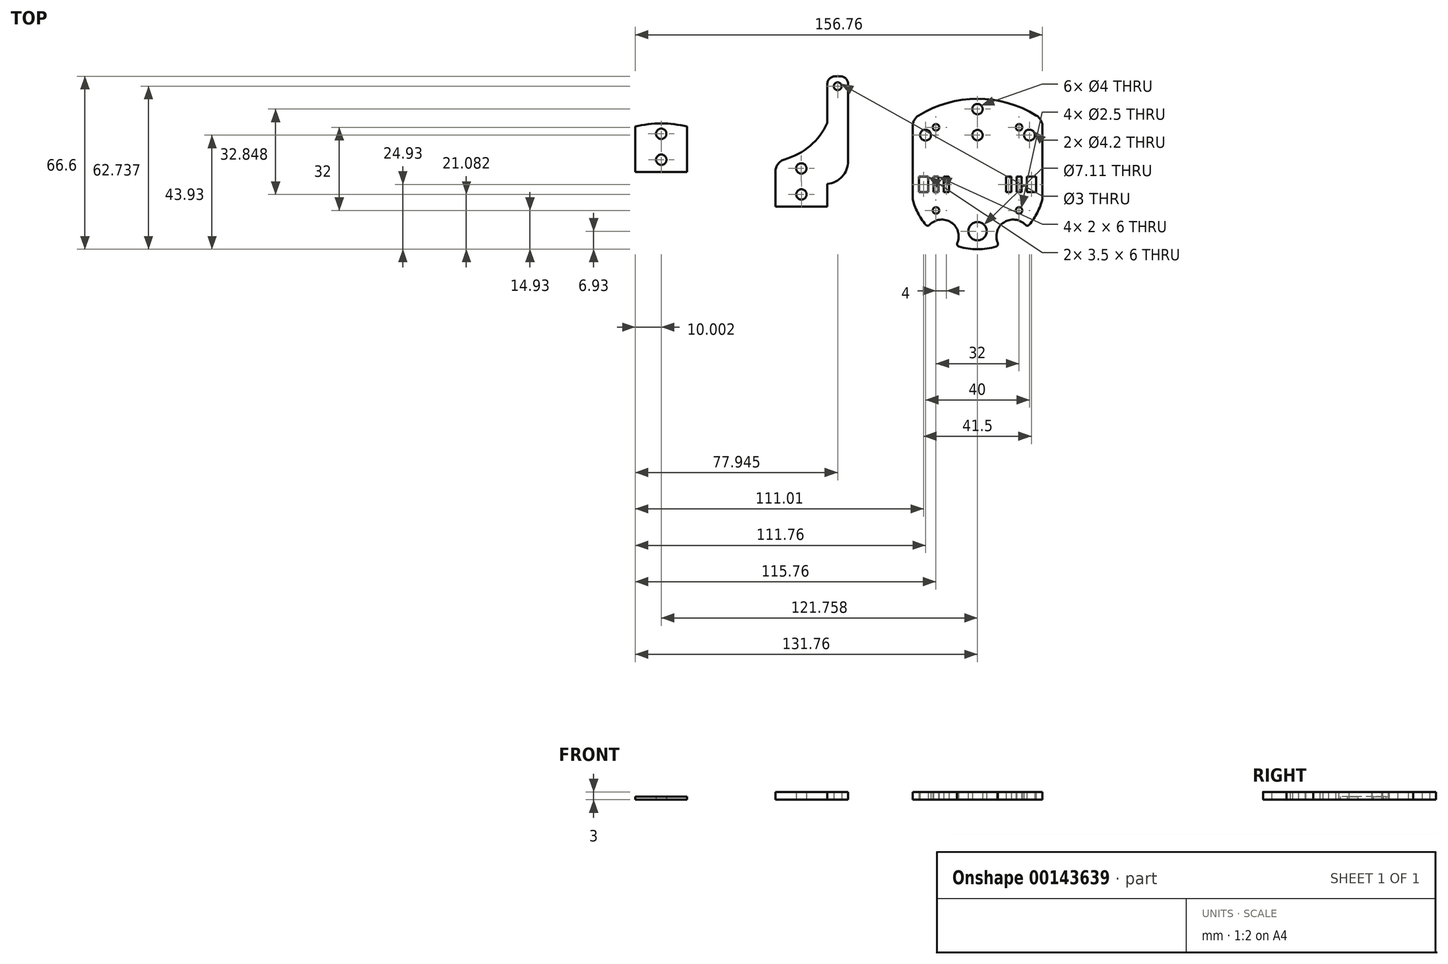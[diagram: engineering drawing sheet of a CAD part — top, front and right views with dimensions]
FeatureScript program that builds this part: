
annotation { "Feature Type Name" : "Feature", "Feature Type Description" : "" }
export const myFeature = defineFeature(function(context is Context, id is Id, definition is map)
    precondition{}
    {
        {
            var Q0;
            Q0=qCreatedBy(makeId("Top.planeOp"),FACE);
            var sketch = newSketch(context, id + "F0", { "sketchPlane" : qUnion([Q0])});
            skPoint(sketch, "E0.middle", {"position": v(0, 0) * mm});
            skLineSegment(sketch, "E1.top", {"start": v(-25, -10.03) * mm, "end": v(22.32, -10.03) * mm, "construction": true});
            skLineSegment(sketch, "E2.bottom", {"start": v(-20, 19) * mm, "end": v(20, 19) * mm, "construction": true});
            skCircle(sketch, "E3", {"center": v(-20, 19) * mm, "radius": 10 * mm, "construction": true});
            skCircle(sketch, "E4", {"center": v(0, -18) * mm, "radius": 10 * mm, "construction": true});
            skLineSegment(sketch, "E5.left", {"start": v(-25, 22.31) * mm, "end": v(-25, -5.6) * mm});
            skLineSegment(sketch, "E5.right", {"start": v(25, 22.31) * mm, "end": v(25, -5.6) * mm});
            skCircle(sketch, "E6", {"center": v(0, -18) * mm, "radius": 3.56 * mm});
            skCircle(sketch, "E7", {"center": v(-20, 19) * mm, "radius": 2.1 * mm});
            skCircle(sketch, "E8", {"center": v(20, 19) * mm, "radius": 2.1 * mm});
            skLineSegment(sketch, "E9", {"start": v(0, 0) * mm, "end": v(-25, 0) * mm, "construction": true});
            skLineSegment(sketch, "E10", {"start": v(0, 0) * mm, "end": v(0, 25) * mm, "construction": true});
            skLineSegment(sketch, "E11.bottom", {"start": v(-19, 3) * mm, "end": v(-22.5, 3) * mm});
            skLineSegment(sketch, "E11.top", {"start": v(-19, -3) * mm, "end": v(-22.5, -3) * mm});
            skLineSegment(sketch, "E11.left", {"start": v(-19, 3) * mm, "end": v(-19, -3) * mm});
            skLineSegment(sketch, "E11.right", {"start": v(-22.5, 3) * mm, "end": v(-22.5, -3) * mm});
            skPoint(sketch, "E11.middle", {"position": v(-20.75, 0) * mm});
            skLineSegment(sketch, "E12.bottom", {"start": v(-15, 3) * mm, "end": v(-17, 3) * mm});
            skLineSegment(sketch, "E12.top", {"start": v(-15, -3) * mm, "end": v(-17, -3) * mm});
            skLineSegment(sketch, "E12.left", {"start": v(-15, 3) * mm, "end": v(-15, -3) * mm});
            skLineSegment(sketch, "E12.right", {"start": v(-17, 3) * mm, "end": v(-17, -3) * mm});
            skPoint(sketch, "E12.middle", {"position": v(-16, 0) * mm});
            skLineSegment(sketch, "E13.bottom", {"start": v(-13, 3) * mm, "end": v(-11, 3) * mm});
            skLineSegment(sketch, "E13.top", {"start": v(-13, -3) * mm, "end": v(-11, -3) * mm});
            skLineSegment(sketch, "E13.left", {"start": v(-13, 3) * mm, "end": v(-13, -3) * mm});
            skLineSegment(sketch, "E13.right", {"start": v(-11, 3) * mm, "end": v(-11, -3) * mm});
            skPoint(sketch, "E13.middle", {"position": v(-12, 0) * mm});
            skLineSegment(sketch, "E14.MirrorCS", {"start": v(15, 3) * mm, "end": v(17, 3) * mm});
            skLineSegment(sketch, "E15.MirrorCS", {"start": v(13, -3) * mm, "end": v(11, -3) * mm});
            skLineSegment(sketch, "E16.MirrorCS", {"start": v(11, 3) * mm, "end": v(11, -3) * mm});
            skLineSegment(sketch, "E17.MirrorCS", {"start": v(13, 3) * mm, "end": v(11, 3) * mm});
            skPoint(sketch, "E18.MirrorP", {"position": v(16, 0) * mm});
            skLineSegment(sketch, "E19.MirrorCS", {"start": v(0, 0) * mm, "end": v(25, 0) * mm, "construction": true});
            skLineSegment(sketch, "E20.MirrorCS", {"start": v(22.5, 3) * mm, "end": v(22.5, -3) * mm});
            skLineSegment(sketch, "E21.MirrorCS", {"start": v(13, 3) * mm, "end": v(13, -3) * mm});
            skLineSegment(sketch, "E22.MirrorCS", {"start": v(15, 3) * mm, "end": v(15, -3) * mm});
            skLineSegment(sketch, "E23.MirrorCS", {"start": v(19, 3) * mm, "end": v(22.5, 3) * mm});
            skPoint(sketch, "E24.MirrorP", {"position": v(12, 0) * mm});
            skLineSegment(sketch, "E25.MirrorCS", {"start": v(19, 3) * mm, "end": v(19, -3) * mm});
            skLineSegment(sketch, "E26.MirrorCS", {"start": v(17, 3) * mm, "end": v(17, -3) * mm});
            skPoint(sketch, "E27.MirrorP", {"position": v(20.75, 0) * mm});
            skLineSegment(sketch, "E28.MirrorCS", {"start": v(19, -3) * mm, "end": v(22.5, -3) * mm});
            skLineSegment(sketch, "E29", {"start": v(15, -3) * mm, "end": v(17, -3) * mm});
            skCircle(sketch, "E30", {"center": v(0, 19) * mm, "radius": 2 * mm});
            skCircle(sketch, "E31", {"center": v(0, 29) * mm, "radius": 2 * mm});
            skLineSegment(sketch, "E32", {"start": v(0, 25) * mm, "end": v(0, 29) * mm, "construction": true});
            skArc(sketch, "E33", {"start": v(22.62, 26.57) * mm, "mid": v(0, 32.96) * mm, "end": v(-22.62, 26.57) * mm});
            skPoint(sketch, "E34", {"position": v(-20, 9) * mm});
            skPoint(sketch, "E35", {"position": v(-20, 10) * mm});
            skPoint(sketch, "E36.visualSharp", {"position": v(-25, -10.03) * mm});
            skPoint(sketch, "E37.visualSharp", {"position": v(-8, -24) * mm});
            skPoint(sketch, "E38", {"position": v(0, -8) * mm});
            skPoint(sketch, "E39", {"position": v(0, -10) * mm});
            skPoint(sketch, "E40.visualSharp", {"position": v(-25, 25) * mm});
            skArc(sketch, "E40.filletArc", {"start": v(-22.62, 26.57) * mm, "mid": v(-24.36, 24.75) * mm, "end": v(-25, 22.31) * mm});
            skPoint(sketch, "E41.visualSharp", {"position": v(25, 25) * mm});
            skArc(sketch, "E41.filletArc", {"start": v(25, 22.31) * mm, "mid": v(24.36, 24.75) * mm, "end": v(22.62, 26.57) * mm});
            skLineSegment(sketch, "E42.bottom", {"start": v(16, 22) * mm, "end": v(-16, 22) * mm, "construction": true});
            skLineSegment(sketch, "E42.top", {"start": v(16, -10) * mm, "end": v(-16, -10) * mm, "construction": true});
            skLineSegment(sketch, "E42.left", {"start": v(16, 22) * mm, "end": v(16, -10) * mm, "construction": true});
            skLineSegment(sketch, "E42.right", {"start": v(-16, 22) * mm, "end": v(-16, -10) * mm, "construction": true});
            skPoint(sketch, "E42.middle", {"position": v(0, 6) * mm});
            skCircle(sketch, "E43", {"center": v(-16, -10) * mm, "radius": 1.25 * mm});
            skCircle(sketch, "E44", {"center": v(16, -10) * mm, "radius": 1.25 * mm});
            skCircle(sketch, "E45", {"center": v(16, 22) * mm, "radius": 1.25 * mm});
            skCircle(sketch, "E46", {"center": v(-16, 22) * mm, "radius": 1.25 * mm});
            skPoint(sketch, "E47.orphan", {"position": v(25, -10.03) * mm});
            skPoint(sketch, "E48.orphan", {"position": v(8, -24) * mm});
            skLineSegment(sketch, "E49", {"start": v(-25, 14.31) * mm, "end": v(25, 14.31) * mm});
            skPoint(sketch, "E50.visualSharp", {"position": v(-21.13, -10.47) * mm});
            skArc(sketch, "E51", {"start": v(-25, -5.6) * mm, "mid": v(-23.01, -10.83) * mm, "end": v(-19.94, -15.51) * mm});
            skLineSegment(sketch, "E52", {"start": v(0, -18) * mm, "end": v(0, -24.93) * mm, "construction": true});
            skArc(sketch, "E53", {"start": v(0, -24.93) * mm, "mid": v(3.6, -24.67) * mm, "end": v(7.14, -23.92) * mm});
            skArc(sketch, "E54", {"start": v(-7.79, -22.56) * mm, "mid": v(-10.18, -14.59) * mm, "end": v(-18.44, -15.56) * mm});
            skArc(sketch, "E55.MirrorCS", {"start": v(7.79, -22.56) * mm, "mid": v(10.18, -14.59) * mm, "end": v(18.44, -15.56) * mm});
            skArc(sketch, "E56.trimOffspring", {"start": v(-7.14, -23.92) * mm, "mid": v(-3.6, -24.67) * mm, "end": v(0, -24.93) * mm});
            skArc(sketch, "E57.trimOffspring", {"start": v(19.94, -15.51) * mm, "mid": v(23.01, -10.83) * mm, "end": v(25, -5.6) * mm});
            skPoint(sketch, "E58.visualSharp", {"position": v(-19.14, -16.44) * mm});
            skArc(sketch, "E58.filletArc", {"start": v(-19.94, -15.51) * mm, "mid": v(-19.2, -15.88) * mm, "end": v(-18.44, -15.56) * mm});
            skPoint(sketch, "E59.visualSharp", {"position": v(-8.32, -23.55) * mm});
            skArc(sketch, "E59.filletArc", {"start": v(-7.79, -22.56) * mm, "mid": v(-7.77, -23.38) * mm, "end": v(-7.14, -23.92) * mm});
            skPoint(sketch, "E60.visualSharp", {"position": v(8.32, -23.55) * mm});
            skArc(sketch, "E60.filletArc", {"start": v(7.14, -23.92) * mm, "mid": v(7.77, -23.38) * mm, "end": v(7.79, -22.56) * mm});
            skPoint(sketch, "E61.visualSharp", {"position": v(19.14, -16.44) * mm});
            skArc(sketch, "E61.filletArc", {"start": v(18.44, -15.56) * mm, "mid": v(19.2, -15.88) * mm, "end": v(19.94, -15.51) * mm});
            skCircle(sketch, "E62", {"center": v(-121.74, 9.5) * mm, "radius": 2 * mm});
            skCircle(sketch, "E63", {"center": v(-121.76, 19.5) * mm, "radius": 2 * mm});
            skLineSegment(sketch, "E64", {"start": v(-121.76, 15.5) * mm, "end": v(-121.76, 19.5) * mm, "construction": true});
            skArc(sketch, "E65", {"start": v(-111.76, 22.3) * mm, "mid": v(-121.76, 23.47) * mm, "end": v(-131.76, 22.3) * mm});
            skLineSegment(sketch, "E66", {"start": v(-131.76, 4.82) * mm, "end": v(-111.76, 4.82) * mm});
            skLineSegment(sketch, "E67.left", {"start": v(-111.76, 22.3) * mm, "end": v(-111.76, 4.82) * mm});
            skLineSegment(sketch, "E67.right", {"start": v(-131.76, 22.3) * mm, "end": v(-131.76, 4.82) * mm});
            skPoint(sketch, "E67.middle", {"position": v(-121.76, 15.5) * mm});
            skCircle(sketch, "E68", {"center": v(-67.8, -3.85) * mm, "radius": 2 * mm});
            skCircle(sketch, "E69", {"center": v(-67.81, 6.15) * mm, "radius": 2 * mm});
            skLineSegment(sketch, "E70", {"start": v(-67.81, 2.15) * mm, "end": v(-67.81, 6.15) * mm, "construction": true});
            skLineSegment(sketch, "E71", {"start": v(-77.81, -8.53) * mm, "end": v(-57.81, -8.53) * mm});
            skLineSegment(sketch, "E72.left", {"start": v(-57.81, 0.2) * mm, "end": v(-57.81, -8.53) * mm});
            skLineSegment(sketch, "E72.right", {"start": v(-77.81, 4.87) * mm, "end": v(-77.81, -8.53) * mm});
            skPoint(sketch, "E72.middle", {"position": v(-67.81, 2.15) * mm});
            skLineSegment(sketch, "E73.top", {"start": v(-54.81, 41.67) * mm, "end": v(-52.81, 41.67) * mm});
            skLineSegment(sketch, "E73.left", {"start": v(-57.81, 23.67) * mm, "end": v(-57.81, 38.67) * mm});
            skLineSegment(sketch, "E73.right", {"start": v(-49.81, 8.94) * mm, "end": v(-49.81, 38.67) * mm});
            skCircle(sketch, "E74", {"center": v(-53.81, 37.8) * mm, "radius": 1.5 * mm});
            skPoint(sketch, "E74.centerSnap0", {"position": v(-53.81, 41.67) * mm});
            skPoint(sketch, "E75.orphan", {"position": v(-57.81, 5.67) * mm});
            skArc(sketch, "E76", {"start": v(-74.16, 9.68) * mm, "mid": v(-64.45, 14.87) * mm, "end": v(-57.81, 23.67) * mm});
            skArc(sketch, "E77", {"start": v(-57.81, 0.2) * mm, "mid": v(-52.12, 3.02) * mm, "end": v(-49.81, 8.94) * mm});
            skPoint(sketch, "E78.visualSharp", {"position": v(-77.81, 8.94) * mm});
            skArc(sketch, "E78.filletArc", {"start": v(-74.16, 9.68) * mm, "mid": v(-76.8, 7.9) * mm, "end": v(-77.81, 4.87) * mm});
            skPoint(sketch, "E79.visualSharp", {"position": v(-57.81, 41.67) * mm});
            skArc(sketch, "E79.filletArc", {"start": v(-54.81, 41.67) * mm, "mid": v(-56.94, 40.79) * mm, "end": v(-57.81, 38.67) * mm});
            skPoint(sketch, "E80.visualSharp", {"position": v(-49.81, 41.67) * mm});
            skArc(sketch, "E80.filletArc", {"start": v(-49.81, 38.67) * mm, "mid": v(-50.7, 40.79) * mm, "end": v(-52.81, 41.67) * mm});
            skSolve(sketch);
        }
        {
            var Q0;
            Q0=makeQuery(id+"F0.imprint","IMPRINT",FACE,{"disambiguationData":[TD([[makeQuery(id+"F0.imprint","IMPRINT",EDGE,{"derivedFrom":sQuery(id+"F0.wireOp",EDGE,"E6")}),-1.0]])]});
            var Q1;
            Q1=makeQuery(id+"F0.imprint","IMPRINT",FACE,{"disambiguationData":[TD([[makeQuery(id+"F0.imprint","IMPRINT",EDGE,{"derivedFrom":sQuery(id+"F0.wireOp",EDGE,"E7")}),-1.0]])]});
            var Q2;
            Q2=makeQuery(id+"F0.imprint","IMPRINT",FACE,{"disambiguationData":[TD([[makeQuery(id+"F0.imprint","IMPRINT",EDGE,{"derivedFrom":sQuery(id+"F0.wireOp",EDGE,"AnCcxth8-TEnw-8CJA-Q1e5-bC0U5bzkQu75")}),1.0]])]});
            var Q3;
            {var subQ3=sQuery(id+"F0.wireOp",EDGE,"c200fd2f-bd05-45dd-b6f9-3ae92d8b672b0.MirrorCS");Q3=makeQuery(id+"F0.imprint","IMPRINT",FACE,{"disambiguationData":[TD([[makeQuery(id+"F0.imprint","IMPRINT",EDGE,{"derivedFrom":subQ3}),-1.0]])]});}
            var Q4;
            {var subQ0=sQuery(id+"F0.wireOp",EDGE,"69943f32-f5be-4bb6-8905-9935c4f36ada.filletArc");Q4=makeQuery(id+"F0.imprint","IMPRINT",FACE,{"disambiguationData":[TD([[makeQuery(id+"F0.imprint","IMPRINT",EDGE,{"derivedFrom":subQ0}),1.0]])]});}
            var Q5;
            {var subQ1=sQuery(id+"F0.wireOp",EDGE,"1c1e505f-d3b0-43af-af64-12dd094d3fbb0.MirrorCS");var subQ3=sQuery(id+"F0.wireOp",EDGE,"ab5f363a-6a9b-4e83-99b5-ab17280f4d850.MirrorCS");var subQ4=makeQuery(id+"F0.imprint","INTERSECT",VERTEX,{"disambiguationData":[OD(0.0)],"derivedFrom":[subQ1,subQ3]});Q5=makeQuery(id+"F0.imprint","IMPRINT",FACE,{"disambiguationData":[TD([[makeQuery(id+"F0.imprint","IMPRINT",EDGE,{"disambiguationData":[TD([[subQ4,-1.0]])],"derivedFrom":subQ3}),-1.0]])]});}
            var Q6;
            Q6=makeQuery(id+"F0.imprint","IMPRINT",FACE,{"disambiguationData":[TD([[makeQuery(id+"F0.imprint","IMPRINT",EDGE,{"derivedFrom":sQuery(id+"F0.wireOp",EDGE,"E68")}),-1.0]])]});
            extrude(context, id + "F1", {"entities" : qUnion([Q0, Q1, Q2, Q3, Q4, Q5, Q6]), "depth" : 3 * mm});
        }
        {
            var Q0;
            Q0=makeQuery(id+"F0.imprint","IMPRINT",FACE,{"disambiguationData":[TD([[makeQuery(id+"F0.imprint","IMPRINT",EDGE,{"derivedFrom":sQuery(id+"F0.wireOp",EDGE,"E7")}),-1.0]])]});
            var Q1;
            Q1=makeQuery(id+"F0.imprint","IMPRINT",FACE,{"disambiguationData":[TD([[makeQuery(id+"F0.imprint","IMPRINT",EDGE,{"derivedFrom":sQuery(id+"F0.wireOp",EDGE,"E46")}),1.0]])]});
            var Q2;
            Q2=makeQuery(id+"F0.imprint","IMPRINT",FACE,{"disambiguationData":[TD([[makeQuery(id+"F0.imprint","IMPRINT",EDGE,{"derivedFrom":sQuery(id+"F0.wireOp",EDGE,"E45")}),1.0]])]});
            extrude(context, id + "F2", {"entities" : qUnion([Q0, Q1, Q2]), "depth" : 3 * mm});
        }
        {
            var Q0;
            Q0=makeQuery(id+"F2.opExtrude","SWEPT_BODY",BODY,{"disambiguationData":[OSD([sQuery(id+"F0.wireOp",EDGE,"E5.left"),sQuery(id+"F0.wireOp",EDGE,"E5.right"),sQuery(id+"F0.wireOp",EDGE,"E7"),sQuery(id+"F0.wireOp",EDGE,"E8"),sQuery(id+"F0.wireOp",EDGE,"E30"),sQuery(id+"F0.wireOp",EDGE,"E31"),sQuery(id+"F0.wireOp",EDGE,"E33"),sQuery(id+"F0.wireOp",EDGE,"E40.filletArc"),sQuery(id+"F0.wireOp",EDGE,"E41.filletArc"),sQuery(id+"F0.wireOp",EDGE,"E45"),sQuery(id+"F0.wireOp",EDGE,"E46"),sQuery(id+"F0.wireOp",EDGE,"E49")])]});
            transform(context, id + "F3", {"entities" : qUnion([Q0]), "transformType" : TransformType.TRANSLATION_3D, "dx" : 55.75 * mm, "dy" : 0 * mm, "dz" : 0 * mm, "makeCopy" : false});
        }
        {
            var Q0;
            Q0=makeQuery(id+"F2.opExtrude","CAP_FACE",FACE,{"disambiguationData":[OSD([sQuery(id+"F0.wireOp",EDGE,"E5.left"),sQuery(id+"F0.wireOp",EDGE,"E5.right"),sQuery(id+"F0.wireOp",EDGE,"E7"),sQuery(id+"F0.wireOp",EDGE,"E8"),sQuery(id+"F0.wireOp",EDGE,"E30"),sQuery(id+"F0.wireOp",EDGE,"E31"),sQuery(id+"F0.wireOp",EDGE,"E33"),sQuery(id+"F0.wireOp",EDGE,"E40.filletArc"),sQuery(id+"F0.wireOp",EDGE,"E41.filletArc"),sQuery(id+"F0.wireOp",EDGE,"E49")])],"isStart":false});
            var sketch = newSketch(context, id + "F4", { "sketchPlane" : qUnion([Q0])});
            skLineSegment(sketch, "E81", {"start": v(55.75, 14.31) * mm, "end": v(55.75, 19) * mm, "construction": true});
            skLineSegment(sketch, "E82", {"start": v(55.75, 19) * mm, "end": v(42.75, 19) * mm, "construction": true});
            skCircle(sketch, "E83", {"center": v(42.75, 19) * mm, "radius": 10 * mm, "construction": true});
            skCircle(sketch, "E84", {"center": v(42.75, 19) * mm, "radius": 2.25 * mm});
            skCircle(sketch, "E85.MirrorC", {"center": v(68.75, 19) * mm, "radius": 2.25 * mm});
            skArc(sketch, "E86.MirrorCS", {"start": v(62.92, 31.63) * mm, "mid": v(70.65, 24.5) * mm, "end": v(73.2, 14.3) * mm});
            skLineSegment(sketch, "E87", {"start": v(45.75, 13.74) * mm, "end": v(45.75, 25.76) * mm});
            skPoint(sketch, "E88.newPointB", {"position": v(38.3, 14.3) * mm});
            skArc(sketch, "E89", {"start": v(62.92, 31.63) * mm, "mid": v(54.9, 32.88) * mm, "end": v(47.49, 29.55) * mm});
            skPoint(sketch, "E90.visualSharp", {"position": v(45.75, 27.76) * mm});
            skArc(sketch, "E90.filletArc", {"start": v(47.49, 29.55) * mm, "mid": v(46.2, 27.84) * mm, "end": v(45.75, 25.76) * mm});
            skSolve(sketch);
        }
        {
            var Q0;
            {var subQ2=sQuery(id+"F4.wireOp",EDGE,"W537BFPO-2DYj-tqX4-z8I5-l5NQawsHajvo");Q0=makeQuery(id+"F4.imprint","IMPRINT",FACE,{"disambiguationData":[TD([[makeQuery(id+"F4.imprint","IMPRINT",EDGE,{"derivedFrom":subQ2}),-1.0]])]});}
            var Q1;
            Q1=makeQuery(id+"F4.imprint","IMPRINT",FACE,{"disambiguationData":[TD([[makeQuery(id+"F4.imprint","IMPRINT",EDGE,{"derivedFrom":sQuery(id+"F4.wireOp",EDGE,"E84")}),1.0]])]});
            var Q2;
            Q2=makeQuery(id+"F4.imprint","IMPRINT",FACE,{"disambiguationData":[TD([[makeQuery(id+"F4.imprint","IMPRINT",EDGE,{"derivedFrom":sQuery(id+"F4.wireOp",EDGE,"E85.MirrorC")}),-1.0]])]});
            var Q3;
            {var subQ3=sQuery(id+"F4.wireOp",EDGE,"E86.MirrorCS");Q3=makeQuery(id+"F4.imprint","IMPRINT",FACE,{"disambiguationData":[TD([[makeQuery(id+"F4.imprint","IMPRINT",EDGE,{"derivedFrom":subQ3}),1.0]])]});}
            var Q4;
            Q4=makeQuery(id+"F4.imprint","IMPRINT",FACE,{"disambiguationData":[TD([[makeQuery(id+"F4.imprint","IMPRINT",EDGE,{"derivedFrom":sQuery(id+"F4.wireOp",EDGE,"E84")}),-1.0]])]});
            extrude(context, id + "F5", {"entities" : qUnion([Q0, Q1, Q2, Q3, Q4]), "operationType" : NewBodyOperationType.REMOVE, "oppositeDirection" : true, "depth" : 25 * mm});
        }
        {
            var Q0;
            Q0=makeQuery(id+"F0.imprint","IMPRINT",FACE,{"disambiguationData":[TD([[makeQuery(id+"F0.imprint","IMPRINT",EDGE,{"derivedFrom":sQuery(id+"F0.wireOp",EDGE,"E62")}),-1.0]])]});
            extrude(context, id + "F6", {"entities" : qUnion([Q0]), "depth" : 1.25 * mm});
        }
        {
            var Q0;
            Q0=makeQuery(id+"F2.opExtrude","SWEPT_BODY",BODY,{"disambiguationData":[OSD([sQuery(id+"F0.wireOp",EDGE,"E5.left"),sQuery(id+"F0.wireOp",EDGE,"E5.right"),sQuery(id+"F0.wireOp",EDGE,"E7"),sQuery(id+"F0.wireOp",EDGE,"E8"),sQuery(id+"F0.wireOp",EDGE,"E30"),sQuery(id+"F0.wireOp",EDGE,"E31"),sQuery(id+"F0.wireOp",EDGE,"E33"),sQuery(id+"F0.wireOp",EDGE,"E40.filletArc"),sQuery(id+"F0.wireOp",EDGE,"E41.filletArc"),sQuery(id+"F0.wireOp",EDGE,"E49")])]});
            deleteBodies(context, id + "F7", {"entities" : qUnion([Q0])});
        }
    });
